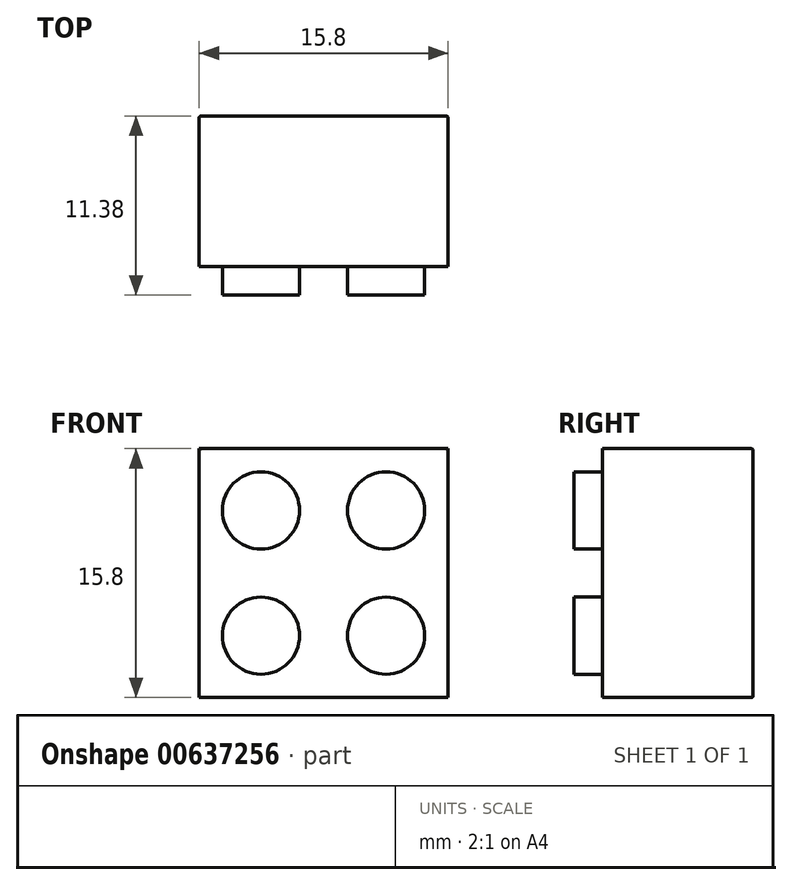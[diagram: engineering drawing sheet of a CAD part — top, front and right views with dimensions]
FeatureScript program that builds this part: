
annotation { "Feature Type Name" : "Feature", "Feature Type Description" : "" }
export const myFeature = defineFeature(function(context is Context, id is Id, definition is map)
    precondition{}
    {
        {
            var Q0;
            Q0=qCreatedBy(makeId("Front.planeOp"),FACE);
            var sketch = newSketch(context, id + "F0", { "sketchPlane" : qUnion([Q0])});
            skLineSegment(sketch, "E0.bottom", {"start": v(0, 15.8) * mm, "end": v(15.8, 15.8) * mm});
            skLineSegment(sketch, "E0.top", {"start": v(0, 0) * mm, "end": v(15.8, 0) * mm});
            skLineSegment(sketch, "E0.left", {"start": v(0, 15.8) * mm, "end": v(0, 0) * mm});
            skLineSegment(sketch, "E0.right", {"start": v(15.8, 15.8) * mm, "end": v(15.8, 0) * mm});
            skSolve(sketch);
        }
        {
            var Q0;
            Q0=qSketchRegion(id+"F0",true);
            extrude(context, id + "F1", {"entities" : qUnion([Q0]), "depth" : 9.55 * mm});
        }
        {
            var Q0;
            Q0=makeQuery(id+"F1.opExtrude","CAP_FACE",FACE,{"disambiguationData":[OSD([sQuery(id+"F0.wireOp",EDGE,"E0.bottom"),sQuery(id+"F0.wireOp",EDGE,"E0.top"),sQuery(id+"F0.wireOp",EDGE,"E0.left"),sQuery(id+"F0.wireOp",EDGE,"E0.right")])],"isStart":false});
            var sketch = newSketch(context, id + "F2", { "sketchPlane" : qUnion([Q0])});
            skCircle(sketch, "E1", {"center": v(3.93, 11.88) * mm, "radius": 2.45 * mm});
            skCircle(sketch, "E2", {"center": v(11.88, 11.88) * mm, "radius": 2.45 * mm});
            skCircle(sketch, "E3", {"center": v(11.88, 3.93) * mm, "radius": 2.45 * mm});
            skCircle(sketch, "E4", {"center": v(3.93, 3.93) * mm, "radius": 2.45 * mm});
            skSolve(sketch);
        }
        {
            var Q0;
            Q0=makeQuery(id+"F2.imprint","IMPRINT",FACE,{"disambiguationData":[TD([[makeQuery(id+"F2.imprint","IMPRINT",EDGE,{"derivedFrom":sQuery(id+"F2.wireOp",EDGE,"E1")}),-1.0]])]});
            var sketch = newSketch(context, id + "F3", { "sketchPlane" : qUnion([Q0])});
            skSolve(sketch);
        }
        {
            var Q0;
            Q0=qSketchRegion(id+"F3",true);
            var Q1;
            Q1=makeQuery(id+"F2.imprint","IMPRINT",FACE,{"disambiguationData":[TD([[makeQuery(id+"F2.imprint","IMPRINT",EDGE,{"derivedFrom":sQuery(id+"F2.wireOp",EDGE,"E1")}),1.0]])]});
            extrude(context, id + "F4", {"entities" : qUnion([Q0, Q1]), "operationType" : NewBodyOperationType.ADD, "depth" : 1.83 * mm});
        }
        {
            var Q0;
            Q0=makeQuery(id+"F3.imprint","IMPRINT",FACE,{"disambiguationData":[TD([[makeQuery(id+"F3.imprint","IMPRINT",EDGE,{"derivedFrom":makeQuery(id+"F2.imprint","IMPRINT",EDGE,{"derivedFrom":sQuery(id+"F2.wireOp",EDGE,"E1")})}),-1.0]])]});
            var sketch = newSketch(context, id + "F5", { "sketchPlane" : qUnion([Q0])});
            skSolve(sketch);
        }
        {
            var Q0;
            Q0=qSketchRegion(id+"F5",true);
            var Q1;
            Q1=makeQuery(id+"F3.imprint","IMPRINT",FACE,{"disambiguationData":[TD([[makeQuery(id+"F3.imprint","IMPRINT",EDGE,{"derivedFrom":makeQuery(id+"F2.imprint","IMPRINT",EDGE,{"derivedFrom":sQuery(id+"F2.wireOp",EDGE,"E2")})}),1.0]])]});
            var Q2;
            Q2=makeQuery(id+"F3.imprint","IMPRINT",FACE,{"disambiguationData":[TD([[makeQuery(id+"F3.imprint","IMPRINT",EDGE,{"derivedFrom":makeQuery(id+"F2.imprint","IMPRINT",EDGE,{"derivedFrom":sQuery(id+"F2.wireOp",EDGE,"E4")})}),1.0]])]});
            var Q3;
            Q3=makeQuery(id+"F3.imprint","IMPRINT",FACE,{"disambiguationData":[TD([[makeQuery(id+"F3.imprint","IMPRINT",EDGE,{"derivedFrom":makeQuery(id+"F2.imprint","IMPRINT",EDGE,{"derivedFrom":sQuery(id+"F2.wireOp",EDGE,"E3")})}),1.0]])]});
            extrude(context, id + "F6", {"entities" : qUnion([Q0, Q1, Q2, Q3]), "operationType" : NewBodyOperationType.ADD, "depth" : 1.83 * mm});
        }
        {
            var Q0;
            Q0=makeQuery(id+"F1.opExtrude","CAP_FACE",FACE,{"disambiguationData":[OSD([sQuery(id+"F0.wireOp",EDGE,"E0.bottom"),sQuery(id+"F0.wireOp",EDGE,"E0.top"),sQuery(id+"F0.wireOp",EDGE,"E0.left"),sQuery(id+"F0.wireOp",EDGE,"E0.right")])],"isStart":true});
            fillet(context, id + "F7", {"entities" : qUnion([Q0]), "radius" : 0.1 * mm, "tangentPropagation" : true, "allowEdgeOverflow" : false});
        }
    });
